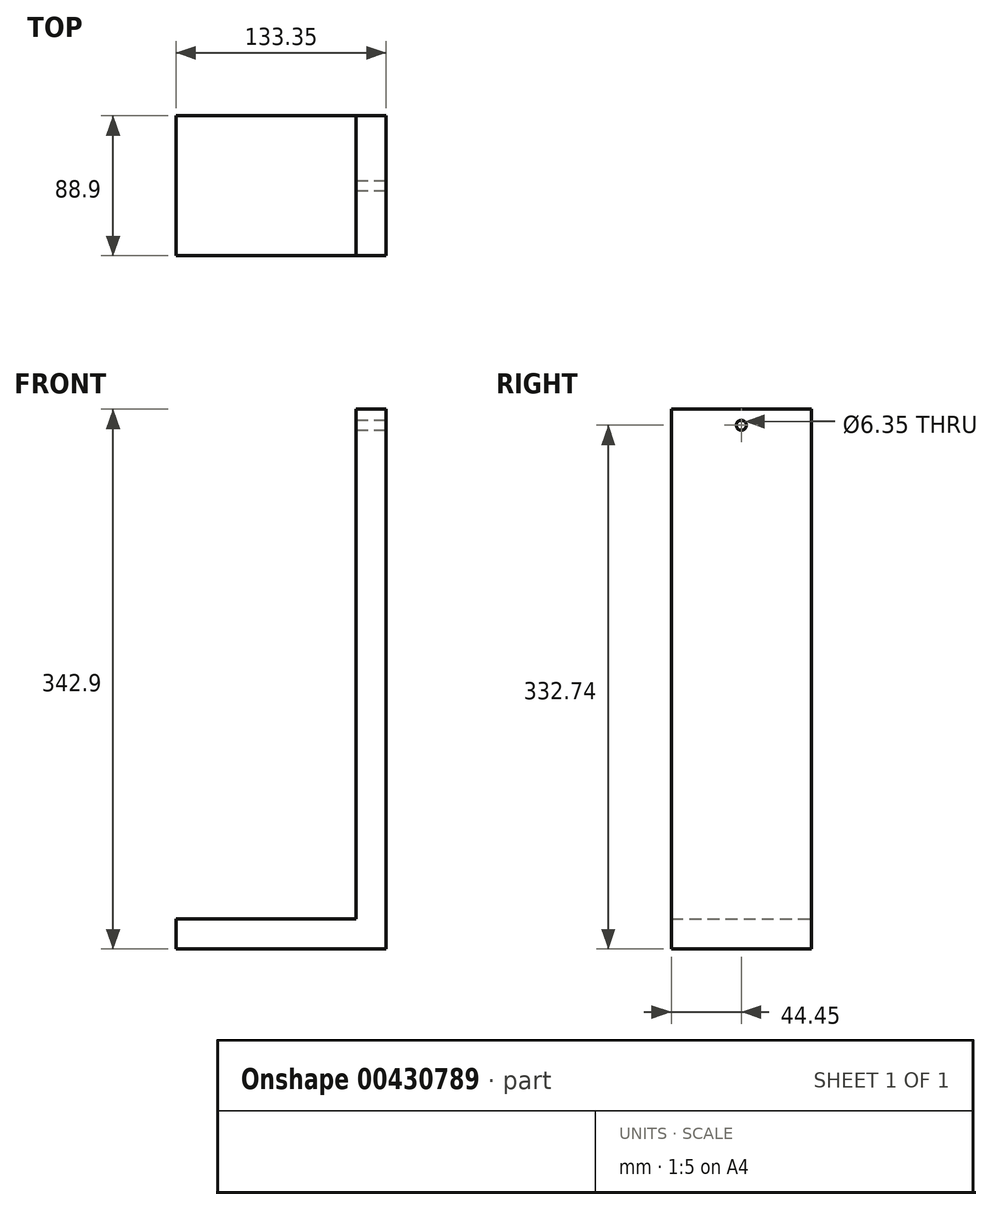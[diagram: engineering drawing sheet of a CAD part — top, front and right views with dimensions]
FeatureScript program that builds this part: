
annotation { "Feature Type Name" : "Feature", "Feature Type Description" : "" }
export const myFeature = defineFeature(function(context is Context, id is Id, definition is map)
    precondition{}
    {
        {
            var Q0;
            Q0=qCreatedBy(makeId("Front.planeOp"),FACE);
            var sketch = newSketch(context, id + "F0", { "sketchPlane" : qUnion([Q0])});
            skLineSegment(sketch, "E0", {"start": v(0, 0) * mm, "end": v(0, 342.9) * mm});
            skLineSegment(sketch, "E1", {"start": v(0, 342.9) * mm, "end": v(-19.05, 342.9) * mm});
            skLineSegment(sketch, "E2", {"start": v(-19.05, 342.9) * mm, "end": v(-19.05, 19.05) * mm});
            skLineSegment(sketch, "E3", {"start": v(-19.05, 19.05) * mm, "end": v(-133.35, 19.05) * mm});
            skLineSegment(sketch, "E4", {"start": v(-133.35, 19.05) * mm, "end": v(-133.35, 0) * mm});
            skLineSegment(sketch, "E5", {"start": v(-133.35, 0) * mm, "end": v(0, 0) * mm});
            skSolve(sketch);
        }
        {
            var Q0;
            Q0=makeQuery(id+"F0.imprint","IMPRINT",FACE,{"disambiguationData":[TD([[makeQuery(id+"F0.imprint","IMPRINT",EDGE,{"derivedFrom":sQuery(id+"F0.wireOp",EDGE,"E0")}),1.0]])]});
            extrude(context, id + "F1", {"entities" : qUnion([Q0]), "depth" : 88.9 * mm});
        }
        {
            var Q0;
            Q0=makeQuery(id+"F1.opExtrude","SWEPT_FACE",FACE,{"disambiguationData":[OSD([sQuery(id+"F0.wireOp",EDGE,"E2")])]});
            var sketch = newSketch(context, id + "F2", { "sketchPlane" : qUnion([Q0])});
            skLineSegment(sketch, "E6", {"start": v(0, 342.9) * mm, "end": v(44.45, 342.9) * mm});
            skLineSegment(sketch, "E7", {"start": v(44.45, 342.9) * mm, "end": v(44.45, 332.74) * mm});
            skSolve(sketch);
        }
        {
            var Q0;
            Q0=sQuery(id+"F2.wireOp",VERTEX,"E7.end");
            var Q1;
            Q1=makeQuery(id+"F1.opExtrude","SWEPT_BODY",BODY,{"disambiguationData":[OSD([sQuery(id+"F0.wireOp",EDGE,"E0"),sQuery(id+"F0.wireOp",EDGE,"E1"),sQuery(id+"F0.wireOp",EDGE,"E2"),sQuery(id+"F0.wireOp",EDGE,"E3"),sQuery(id+"F0.wireOp",EDGE,"E4"),sQuery(id+"F0.wireOp",EDGE,"E5")])]});
            hole(context, id + "F3", {"style" : HoleStyle.SIMPLE, "endStyle" : HoleEndStyle.THROUGH, "holeDiameter" : 6.35 * mm, "isTappedThrough" : true, "tappedDepth" : 12.7 * mm, "tapClearance" : 3, "locations" : qUnion([Q0]), "scope" : qUnion([Q1]), "startStyle" : HoleStartStyle.PART});
        }
    });
